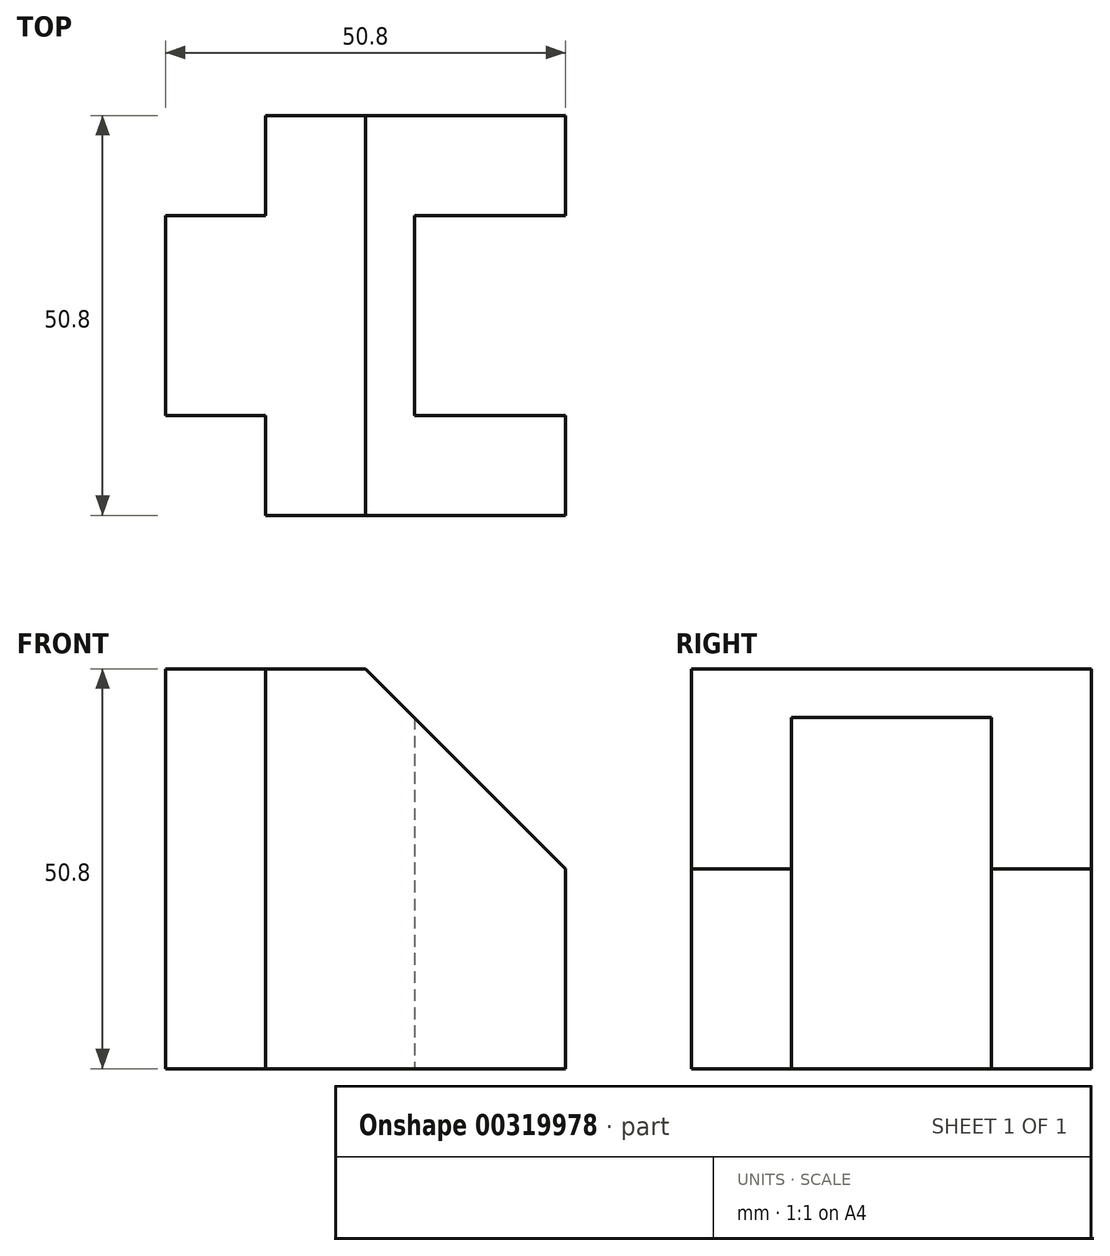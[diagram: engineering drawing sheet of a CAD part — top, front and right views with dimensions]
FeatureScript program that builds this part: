
annotation { "Feature Type Name" : "Feature", "Feature Type Description" : "" }
export const myFeature = defineFeature(function(context is Context, id is Id, definition is map)
    precondition{}
    {
        {
            var Q0;
            Q0=qCreatedBy(makeId("Top.planeOp"),FACE);
            var sketch = newSketch(context, id + "F0", { "sketchPlane" : qUnion([Q0])});
            skLineSegment(sketch, "E0", {"start": v(0, 0) * mm, "end": v(0, 12.7) * mm});
            skLineSegment(sketch, "E1", {"start": v(0, 12.7) * mm, "end": v(-12.7, 12.7) * mm});
            skLineSegment(sketch, "E2", {"start": v(-12.7, 12.7) * mm, "end": v(-12.7, 38.1) * mm});
            skLineSegment(sketch, "E3", {"start": v(-12.7, 38.1) * mm, "end": v(0, 38.1) * mm});
            skLineSegment(sketch, "E4", {"start": v(0, 38.1) * mm, "end": v(0, 50.8) * mm});
            skLineSegment(sketch, "E5", {"start": v(0, 50.8) * mm, "end": v(38.1, 50.8) * mm});
            skLineSegment(sketch, "E6", {"start": v(38.1, 50.8) * mm, "end": v(38.1, 38.1) * mm});
            skLineSegment(sketch, "E7", {"start": v(38.1, 38.1) * mm, "end": v(18.91, 38.1) * mm});
            skLineSegment(sketch, "E8", {"start": v(18.91, 38.1) * mm, "end": v(18.91, 12.7) * mm});
            skLineSegment(sketch, "E9", {"start": v(18.91, 12.7) * mm, "end": v(38.1, 12.7) * mm});
            skLineSegment(sketch, "E10", {"start": v(38.1, 12.7) * mm, "end": v(38.1, 0) * mm});
            skLineSegment(sketch, "E11", {"start": v(38.1, 0) * mm, "end": v(0, 0) * mm});
            skLineSegment(sketch, "E12", {"start": v(12.7, 50.8) * mm, "end": v(12.7, 0) * mm});
            skSolve(sketch);
        }
        {
            var Q0;
            Q0 = qSketchRegion(id + "F0", true);
            extrude(context, id + "F1", {"entities" : qUnion([Q0]), "depth" : 50.8 * mm});
        }
        {
            var Q0;
            Q0=makeQuery(id+"F1.opExtrude","SWEPT_FACE",FACE,{"disambiguationData":[OSD([sQuery(id+"F0.wireOp",EDGE,"E11")])]});
            var sketch = newSketch(context, id + "F2", { "sketchPlane" : qUnion([Q0])});
            skLineSegment(sketch, "E13", {"start": v(38.1, 0) * mm, "end": v(38.1, 25.4) * mm});
            skLineSegment(sketch, "E14", {"start": v(38.1, 25.4) * mm, "end": v(12.7, 50.8) * mm});
            skLineSegment(sketch, "E15", {"start": v(12.7, 50.8) * mm, "end": v(38.1, 50.8) * mm});
            skLineSegment(sketch, "E16", {"start": v(38.1, 50.8) * mm, "end": v(38.1, 25.4) * mm});
            skSolve(sketch);
        }
        {
            var Q0;
            Q0 = qSketchRegion(id + "F2", true);
            extrude(context, id + "F3", {"entities" : qUnion([Q0]), "operationType" : NewBodyOperationType.REMOVE, "endBound" : BoundingType.THROUGH_ALL, "oppositeDirection" : true, "depth" : 25.4 * mm});
        }
    });
